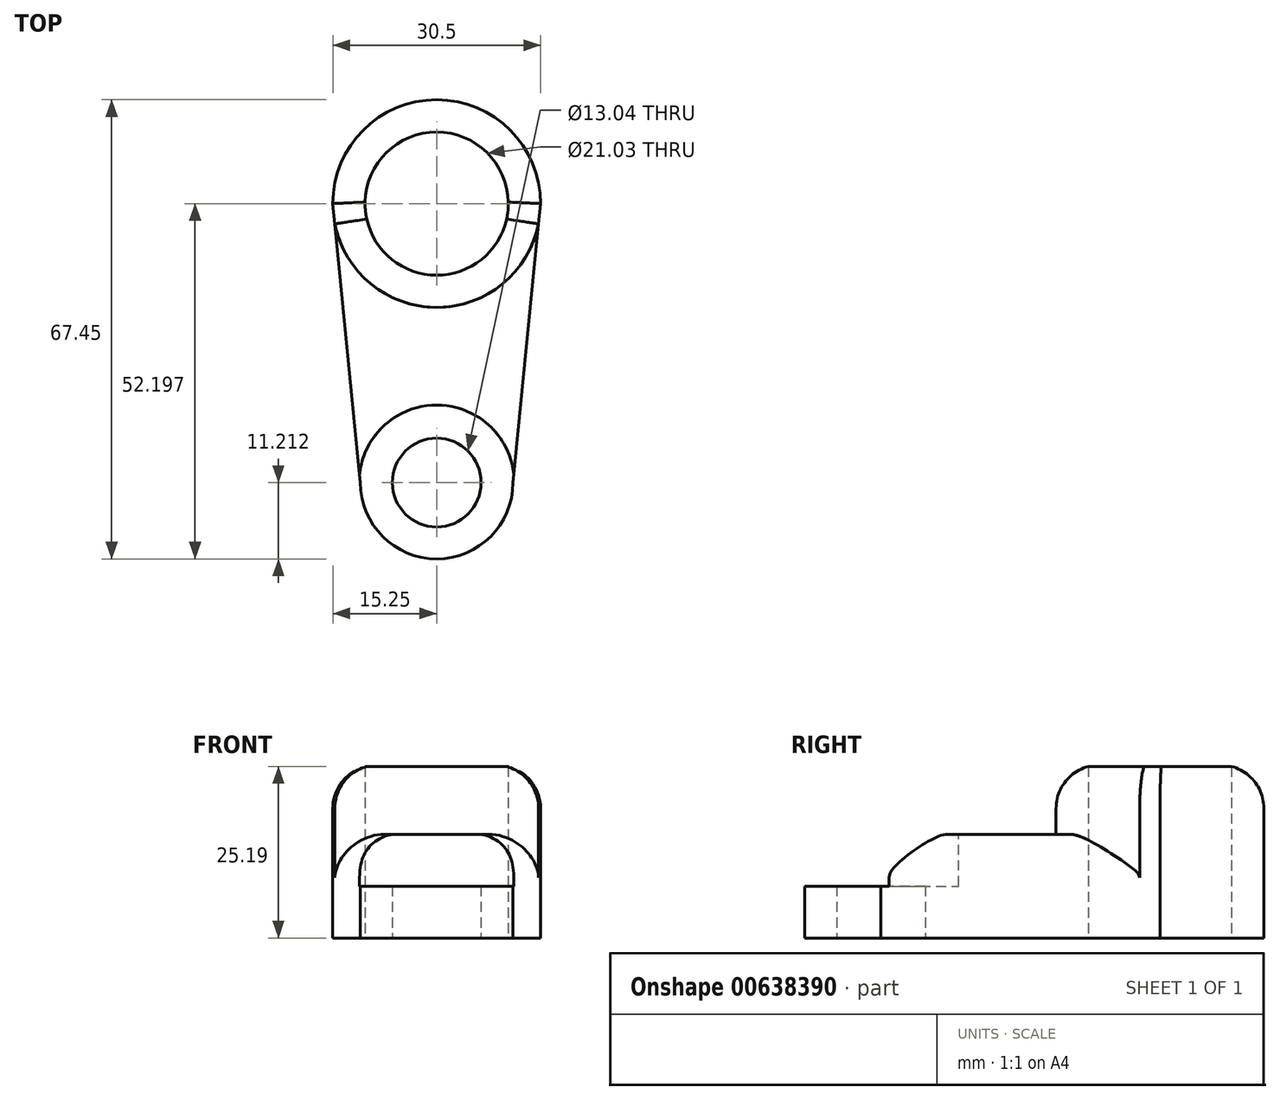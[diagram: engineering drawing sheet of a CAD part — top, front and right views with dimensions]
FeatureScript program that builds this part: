
annotation { "Feature Type Name" : "Feature", "Feature Type Description" : "" }
export const myFeature = defineFeature(function(context is Context, id is Id, definition is map)
    precondition{}
    {
        {
            var Q0;
            Q0=qCreatedBy(makeId("Top.planeOp"),FACE);
            var sketch = newSketch(context, id + "F0", { "sketchPlane" : qUnion([Q0])});
            skLineSegment(sketch, "E0", {"start": v(0, 0) * mm, "end": v(0, 20.48) * mm});
            skLineSegment(sketch, "E1", {"start": v(0, 0) * mm, "end": v(0, -20.5) * mm});
            skCircle(sketch, "E2", {"center": v(0, 20.48) * mm, "radius": 15.25 * mm});
            skCircle(sketch, "E3", {"center": v(0, -20.5) * mm, "radius": 11.2 * mm});
            skCircle(sketch, "E4", {"center": v(0, 20.48) * mm, "radius": 10.52 * mm});
            skCircle(sketch, "E5", {"center": v(0, -20.5) * mm, "radius": 6.52 * mm});
            skLineSegment(sketch, "E6", {"start": v(0, 20.48) * mm, "end": v(-15.25, 20.48) * mm});
            skLineSegment(sketch, "E7", {"start": v(0, 20.48) * mm, "end": v(15.25, 20.48) * mm});
            skLineSegment(sketch, "E8", {"start": v(0, -20.5) * mm, "end": v(11.2, -20.5) * mm});
            skLineSegment(sketch, "E9", {"start": v(0, -20.5) * mm, "end": v(-11.2, -20.5) * mm});
            skLineSegment(sketch, "E10", {"start": v(-15.25, 20.48) * mm, "end": v(-11.2, -20.5) * mm});
            skLineSegment(sketch, "E11", {"start": v(15.25, 20.48) * mm, "end": v(11.2, -20.5) * mm});
            skSolve(sketch);
        }
        {
            var Q0;
            {var subQ0=sQuery(id+"F0.wireOp",EDGE,"E6");var subQ5=sQuery(id+"F0.wireOp",EDGE,"E4");var subQ6=makeQuery(id+"F0.imprint","INTERSECT",VERTEX,{"derivedFrom":[subQ5,subQ0]});Q0=makeQuery(id+"F0.imprint","IMPRINT",FACE,{"disambiguationData":[TD([[makeQuery(id+"F0.imprint","IMPRINT",EDGE,{"disambiguationData":[TD([[subQ6,1.0]])],"derivedFrom":subQ5}),-1.0]])]});}
            var Q1;
            {var subQ1=sQuery(id+"F0.wireOp",EDGE,"E0");var subQ6=sQuery(id+"F0.wireOp",EDGE,"E2");var subQ8=makeQuery(id+"F0.imprint","INTERSECT",VERTEX,{"derivedFrom":[subQ1,subQ6]});Q1=makeQuery(id+"F0.imprint","IMPRINT",FACE,{"disambiguationData":[TD([[makeQuery(id+"F0.imprint","IMPRINT",EDGE,{"disambiguationData":[TD([[subQ8,-1.0]])],"derivedFrom":subQ1}),1.0]])]});}
            var Q2;
            {var subQ2=sQuery(id+"F0.wireOp",EDGE,"E2");var subQ6=sQuery(id+"F0.wireOp",EDGE,"E0");var subQ7=makeQuery(id+"F0.imprint","INTERSECT",VERTEX,{"derivedFrom":[subQ6,subQ2]});Q2=makeQuery(id+"F0.imprint","IMPRINT",FACE,{"disambiguationData":[TD([[makeQuery(id+"F0.imprint","IMPRINT",EDGE,{"disambiguationData":[TD([[subQ7,-1.0]])],"derivedFrom":subQ6}),-1.0]])]});}
            var Q3;
            {var subQ3=sQuery(id+"F0.wireOp",EDGE,"E1");var subQ5=sQuery(id+"F0.wireOp",EDGE,"E0");var subQ6=makeQuery(id+"F0.imprint","INTERSECT",VERTEX,{"derivedFrom":[subQ5,subQ3]});Q3=makeQuery(id+"F0.imprint","IMPRINT",FACE,{"disambiguationData":[TD([[makeQuery(id+"F0.imprint","IMPRINT",EDGE,{"disambiguationData":[TD([[subQ6,-1.0]])],"derivedFrom":subQ5}),-1.0]])]});}
            var Q4;
            {var subQ3=sQuery(id+"F0.wireOp",EDGE,"E1");var subQ7=sQuery(id+"F0.wireOp",EDGE,"E0");var subQ9=makeQuery(id+"F0.imprint","INTERSECT",VERTEX,{"derivedFrom":[subQ7,subQ3]});Q4=makeQuery(id+"F0.imprint","IMPRINT",FACE,{"disambiguationData":[TD([[makeQuery(id+"F0.imprint","IMPRINT",EDGE,{"disambiguationData":[TD([[subQ9,-1.0]])],"derivedFrom":subQ7}),1.0]])]});}
            var Q5;
            {var subQ0=sQuery(id+"F0.wireOp",EDGE,"E3");var subQ1=sQuery(id+"F0.wireOp",EDGE,"E1");var subQ2=makeQuery(id+"F0.imprint","INTERSECT",VERTEX,{"derivedFrom":[subQ1,subQ0]});Q5=makeQuery(id+"F0.imprint","IMPRINT",FACE,{"disambiguationData":[TD([[makeQuery(id+"F0.imprint","IMPRINT",EDGE,{"disambiguationData":[TD([[subQ2,-1.0]])],"derivedFrom":subQ1}),-1.0]])]});}
            var Q6;
            {var subQ0=sQuery(id+"F0.wireOp",EDGE,"E3");var subQ1=sQuery(id+"F0.wireOp",EDGE,"E1");var subQ2=makeQuery(id+"F0.imprint","INTERSECT",VERTEX,{"derivedFrom":[subQ1,subQ0]});Q6=makeQuery(id+"F0.imprint","IMPRINT",FACE,{"disambiguationData":[TD([[makeQuery(id+"F0.imprint","IMPRINT",EDGE,{"disambiguationData":[TD([[subQ2,-1.0]])],"derivedFrom":subQ1}),1.0]])]});}
            var Q7;
            {var subQ0=sQuery(id+"F0.wireOp",EDGE,"E8");var subQ5=sQuery(id+"F0.wireOp",EDGE,"E5");var subQ6=makeQuery(id+"F0.imprint","INTERSECT",VERTEX,{"derivedFrom":[subQ5,subQ0]});Q7=makeQuery(id+"F0.imprint","IMPRINT",FACE,{"disambiguationData":[TD([[makeQuery(id+"F0.imprint","IMPRINT",EDGE,{"disambiguationData":[TD([[subQ6,1.0]])],"derivedFrom":subQ5}),-1.0]])]});}
            extrude(context, id + "F1", {"entities" : qUnion([Q0, Q1, Q2, Q3, Q4, Q5, Q6, Q7]), "depth" : 15.24 * mm, "offsetDistance" : 25.4 * mm});
        }
        {
            var Q0;
            {var subQ0=sQuery(id+"F0.wireOp",EDGE,"E6");var subQ5=sQuery(id+"F0.wireOp",EDGE,"E4");var subQ6=makeQuery(id+"F0.imprint","INTERSECT",VERTEX,{"derivedFrom":[subQ5,subQ0]});Q0=makeQuery(id+"F0.imprint","IMPRINT",FACE,{"disambiguationData":[TD([[makeQuery(id+"F0.imprint","IMPRINT",EDGE,{"disambiguationData":[TD([[subQ6,1.0]])],"derivedFrom":subQ5}),-1.0]])]});}
            var Q1;
            {var subQ2=sQuery(id+"F0.wireOp",EDGE,"E2");var subQ6=sQuery(id+"F0.wireOp",EDGE,"E0");var subQ7=makeQuery(id+"F0.imprint","INTERSECT",VERTEX,{"derivedFrom":[subQ6,subQ2]});Q1=makeQuery(id+"F0.imprint","IMPRINT",FACE,{"disambiguationData":[TD([[makeQuery(id+"F0.imprint","IMPRINT",EDGE,{"disambiguationData":[TD([[subQ7,-1.0]])],"derivedFrom":subQ6}),-1.0]])]});}
            var Q2;
            {var subQ1=sQuery(id+"F0.wireOp",EDGE,"E0");var subQ6=sQuery(id+"F0.wireOp",EDGE,"E2");var subQ8=makeQuery(id+"F0.imprint","INTERSECT",VERTEX,{"derivedFrom":[subQ1,subQ6]});Q2=makeQuery(id+"F0.imprint","IMPRINT",FACE,{"disambiguationData":[TD([[makeQuery(id+"F0.imprint","IMPRINT",EDGE,{"disambiguationData":[TD([[subQ8,-1.0]])],"derivedFrom":subQ1}),1.0]])]});}
            extrude(context, id + "F2", {"entities" : qUnion([Q0, Q1, Q2]), "operationType" : NewBodyOperationType.ADD, "depth" : 25.4 * mm, "offsetDistance" : 25.4 * mm});
        }
        {
            var Q0;
            {var subQ0=sQuery(id+"F0.wireOp",EDGE,"E8");var subQ5=sQuery(id+"F0.wireOp",EDGE,"E5");var subQ6=makeQuery(id+"F0.imprint","INTERSECT",VERTEX,{"derivedFrom":[subQ5,subQ0]});Q0=makeQuery(id+"F0.imprint","IMPRINT",FACE,{"disambiguationData":[TD([[makeQuery(id+"F0.imprint","IMPRINT",EDGE,{"disambiguationData":[TD([[subQ6,1.0]])],"derivedFrom":subQ5}),-1.0]])]});}
            var Q1;
            {var subQ0=sQuery(id+"F0.wireOp",EDGE,"E3");var subQ1=sQuery(id+"F0.wireOp",EDGE,"E1");var subQ2=makeQuery(id+"F0.imprint","INTERSECT",VERTEX,{"derivedFrom":[subQ1,subQ0]});Q1=makeQuery(id+"F0.imprint","IMPRINT",FACE,{"disambiguationData":[TD([[makeQuery(id+"F0.imprint","IMPRINT",EDGE,{"disambiguationData":[TD([[subQ2,-1.0]])],"derivedFrom":subQ1}),1.0]])]});}
            var Q2;
            {var subQ0=sQuery(id+"F0.wireOp",EDGE,"E3");var subQ1=sQuery(id+"F0.wireOp",EDGE,"E1");var subQ2=makeQuery(id+"F0.imprint","INTERSECT",VERTEX,{"derivedFrom":[subQ1,subQ0]});Q2=makeQuery(id+"F0.imprint","IMPRINT",FACE,{"disambiguationData":[TD([[makeQuery(id+"F0.imprint","IMPRINT",EDGE,{"disambiguationData":[TD([[subQ2,-1.0]])],"derivedFrom":subQ1}),-1.0]])]});}
            extrude(context, id + "F3", {"entities" : qUnion([Q0, Q1, Q2]), "operationType" : NewBodyOperationType.ADD, "depth" : 7.62 * mm, "offsetDistance" : 25.4 * mm});
        }
        {
            var Q0;
            Q0=makeQuery(id+"F1.opExtrude","CAP_FACE",FACE,{"disambiguationData":[OSD([sQuery(id+"F0.wireOp",EDGE,"E2"),sQuery(id+"F0.wireOp",EDGE,"E3"),sQuery(id+"F0.wireOp",EDGE,"E4"),sQuery(id+"F0.wireOp",EDGE,"E5"),sQuery(id+"F0.wireOp",EDGE,"E10"),sQuery(id+"F0.wireOp",EDGE,"E11")])],"isStart":false});
            var sketch = newSketch(context, id + "F4", { "sketchPlane" : qUnion([Q0])});
            skCircle(sketch, "E12", {"center": v(0, -20.5) * mm, "radius": 6.54 * mm});
            skCircle(sketch, "E13", {"center": v(0, -20.5) * mm, "radius": 11.4 * mm});
            skSolve(sketch);
        }
        {
            var Q0;
            Q0=makeQuery(id+"F4.imprint","IMPRINT",FACE,{"disambiguationData":[TD([[makeQuery(id+"F4.imprint","IMPRINT",EDGE,{"derivedFrom":sQuery(id+"F4.wireOp",EDGE,"E12")}),-1.0]])]});
            var Q1;
            Q1=makeQuery(id+"F4.imprint","IMPRINT",FACE,{"disambiguationData":[TD([[makeQuery(id+"F4.imprint","IMPRINT",EDGE,{"derivedFrom":makeQuery(id+"F1.opExtrude","CAP_EDGE",EDGE,{"disambiguationData":[OSD([sQuery(id+"F0.wireOp",EDGE,"E5")])],"isStart":false})}),1.0]])]});
            var Q2;
            Q2=makeQuery(id+"F4.imprint","IMPRINT",FACE,{"disambiguationData":[TD([[makeQuery(id+"F4.imprint","IMPRINT",EDGE,{"derivedFrom":sQuery(id+"F4.wireOp",EDGE,"E12")}),1.0]])]});
            extrude(context, id + "F5", {"entities" : qUnion([Q0, Q1, Q2]), "operationType" : NewBodyOperationType.REMOVE, "oppositeDirection" : true, "depth" : 7.62 * mm, "offsetDistance" : 25.4 * mm});
        }
        {
            var Q0;
            Q0=makeQuery(id+"F5.boolean.opBoolean","COPY",EDGE,{"derivedFrom":makeQuery(id+"F5.opExtrude","SWEPT_EDGE",EDGE,{"disambiguationData":[OSD([sQuery(id+"F0.wireOp",EDGE,"E11"),sQuery(id+"F4.wireOp",EDGE,"E13")])]})});
            var Q1;
            Q1=makeQuery(id+"F5.boolean.opBoolean","COPY",EDGE,{"derivedFrom":makeQuery(id+"F5.opExtrude","SWEPT_EDGE",EDGE,{"disambiguationData":[OSD([sQuery(id+"F0.wireOp",EDGE,"E10"),sQuery(id+"F4.wireOp",EDGE,"E13")])]})});
            var Q2;
            {var subQ0=sQuery(id+"F0.wireOp",EDGE,"E2");Q2=makeQuery(id+"F2.opExtrude","CAP_EDGE",EDGE,{"disambiguationData":[OSD([subQ0]),TDD([makeQuery(id+"F0.imprint","IMPRINT",EDGE,{"disambiguationData":[TD([[makeQuery(id+"F0.imprint","INTERSECT",VERTEX,{"derivedFrom":[subQ0,sQuery(id+"F0.wireOp",EDGE,"E10")]}),-1.0]])],"derivedFrom":subQ0}),makeQuery(id+"F0.imprint","IMPRINT",EDGE,{"disambiguationData":[TD([[makeQuery(id+"F0.imprint","INTERSECT",VERTEX,{"derivedFrom":[subQ0,sQuery(id+"F0.wireOp",EDGE,"E11")]}),1.0]])],"derivedFrom":subQ0})])],"isStart":false});}
            var Q3;
            {var subQ0=sQuery(id+"F0.wireOp",EDGE,"E2");Q3=makeQuery(id+"F2.opExtrude","CAP_EDGE",EDGE,{"disambiguationData":[OSD([subQ0]),TDD([makeQuery(id+"F0.imprint","IMPRINT",EDGE,{"disambiguationData":[TD([[makeQuery(id+"F0.imprint","INTERSECT",VERTEX,{"derivedFrom":[subQ0,sQuery(id+"F0.wireOp",EDGE,"E6"),sQuery(id+"F0.wireOp",EDGE,"E10")]}),1.0]])],"derivedFrom":subQ0})])],"isStart":false});}
            var Q4;
            Q4=makeQuery(id+"F2.opExtrude","CAP_EDGE",EDGE,{"disambiguationData":[OSD([sQuery(id+"F0.wireOp",EDGE,"E11")])],"isStart":false});
            var Q5;
            Q5=makeQuery(id+"F2.opExtrude","CAP_EDGE",EDGE,{"disambiguationData":[OSD([sQuery(id+"F0.wireOp",EDGE,"E10")])],"isStart":false});
            var Q6;
            Q6=makeQuery(id+"F1.opExtrude","CAP_EDGE",EDGE,{"disambiguationData":[OSD([sQuery(id+"F0.wireOp",EDGE,"E11")])],"isStart":false});
            var Q7;
            Q7=makeQuery(id+"F1.opExtrude","CAP_EDGE",EDGE,{"disambiguationData":[OSD([sQuery(id+"F0.wireOp",EDGE,"E10")])],"isStart":false});
            fillet(context, id + "F6", {"entities" : qUnion([Q0, Q1, Q2, Q3, Q4, Q5, Q6, Q7]), "radius" : 6.35 * mm, "tangentPropagation" : true, "allowEdgeOverflow" : false});
        }
    });
